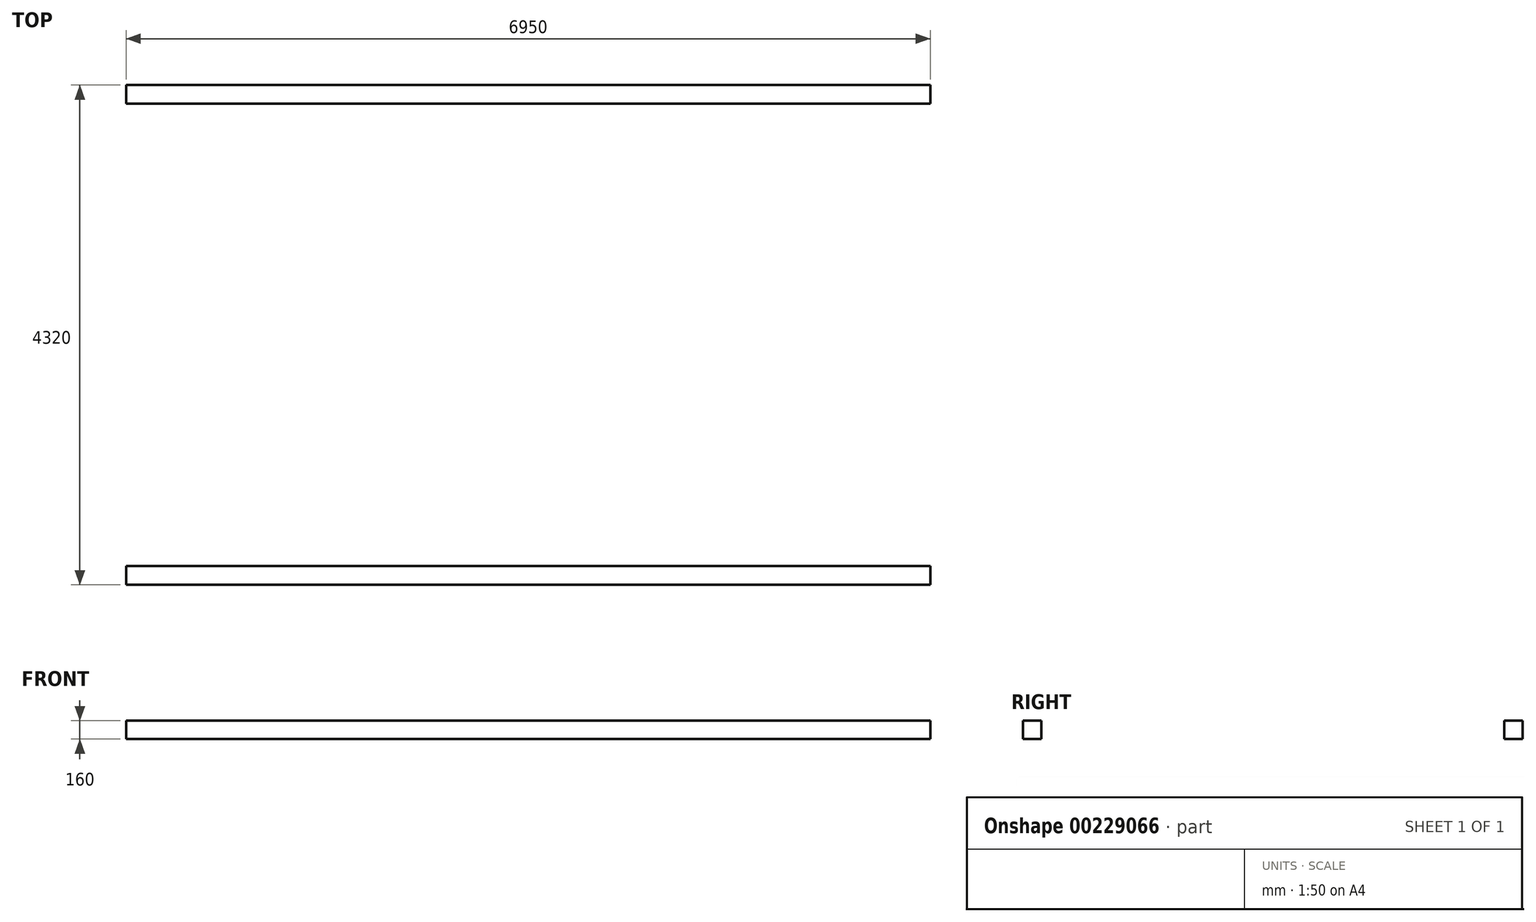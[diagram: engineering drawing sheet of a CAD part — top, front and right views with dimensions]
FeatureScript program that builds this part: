
annotation { "Feature Type Name" : "Feature", "Feature Type Description" : "" }
export const myFeature = defineFeature(function(context is Context, id is Id, definition is map)
    precondition{}
    {
        {
            var Q0;
            Q0=qCreatedBy(makeId("Top.planeOp"),FACE);
            var sketch = newSketch(context, id + "F0", { "sketchPlane" : qUnion([Q0])});
            skLineSegment(sketch, "E0.bottom", {"start": v(-39.6, 45.34) * mm, "end": v(61.47, 45.34) * mm});
            skLineSegment(sketch, "E0.top", {"start": v(-39.6, 50.14) * mm, "end": v(61.47, 50.14) * mm});
            skLineSegment(sketch, "E0.left", {"start": v(-39.6, 45.34) * mm, "end": v(-39.6, 50.14) * mm});
            skLineSegment(sketch, "E0.right", {"start": v(61.47, 45.34) * mm, "end": v(61.47, 50.14) * mm});
            skLineSegment(sketch, "E1.bottom", {"start": v(-39.6, 11.73) * mm, "end": v(61.47, 11.73) * mm});
            skLineSegment(sketch, "E1.top", {"start": v(-39.6, 16) * mm, "end": v(61.47, 16) * mm});
            skLineSegment(sketch, "E1.left", {"start": v(-39.6, 11.73) * mm, "end": v(-39.6, 16) * mm});
            skLineSegment(sketch, "E1.right", {"start": v(61.47, 11.73) * mm, "end": v(61.47, 16) * mm});
            skSolve(sketch);
        }
        {
            var Q0;
            Q0=makeQuery(id+"F0.imprint","IMPRINT",FACE,{"disambiguationData":[TD([[makeQuery(id+"F0.imprint","IMPRINT",EDGE,{"derivedFrom":sQuery(id+"F0.wireOp",EDGE,"E0.bottom")}),1.0]])]});
            var Q1;
            Q1=makeQuery(id+"F0.imprint","IMPRINT",FACE,{"disambiguationData":[TD([[makeQuery(id+"F0.imprint","IMPRINT",EDGE,{"derivedFrom":sQuery(id+"F0.wireOp",EDGE,"E1.bottom")}),1.0]])]});
            extrude(context, id + "F1", {"entities" : qUnion([Q0, Q1]), "depth" : 152.4 * mm});
        }
        {
            var Q0;
            Q0=makeQuery(id+"F1.opExtrude","SWEPT_BODY",BODY,{"disambiguationData":[OSD([sQuery(id+"F0.wireOp",EDGE,"E0.bottom"),sQuery(id+"F0.wireOp",EDGE,"E0.top"),sQuery(id+"F0.wireOp",EDGE,"E0.left"),sQuery(id+"F0.wireOp",EDGE,"E0.right")])]});
            var Q1;
            Q1=makeQuery(id+"F1.opExtrude","SWEPT_BODY",BODY,{"disambiguationData":[OSD([sQuery(id+"F0.wireOp",EDGE,"E1.bottom"),sQuery(id+"F0.wireOp",EDGE,"E1.top"),sQuery(id+"F0.wireOp",EDGE,"E1.left"),sQuery(id+"F0.wireOp",EDGE,"E1.right")])]});
            deleteBodies(context, id + "F2", {"entities" : qUnion([Q0, Q1])});
        }
        {
            var Q0;
            Q0=qCreatedBy(makeId("Top.planeOp"),FACE);
            var sketch = newSketch(context, id + "F3", { "sketchPlane" : qUnion([Q0])});
            skLineSegment(sketch, "E2.bottom", {"start": v(-675.07, 105.87) * mm, "end": v(6274.93, 105.87) * mm});
            skLineSegment(sketch, "E2.top", {"start": v(-675.07, -54.13) * mm, "end": v(6274.93, -54.13) * mm});
            skLineSegment(sketch, "E2.left", {"start": v(-675.07, 105.87) * mm, "end": v(-675.07, -54.13) * mm});
            skLineSegment(sketch, "E2.right", {"start": v(6274.93, 105.87) * mm, "end": v(6274.93, -54.13) * mm});
            skLineSegment(sketch, "E3", {"start": v(-675.07, 4105.87) * mm, "end": v(-675.07, 4265.87) * mm});
            skLineSegment(sketch, "E4", {"start": v(-675.07, 4265.87) * mm, "end": v(6274.93, 4265.87) * mm});
            skLineSegment(sketch, "E5", {"start": v(6274.93, 4265.87) * mm, "end": v(6274.93, 4105.87) * mm});
            skLineSegment(sketch, "E6", {"start": v(6274.93, 4105.87) * mm, "end": v(-675.07, 4105.87) * mm});
            skSolve(sketch);
        }
        {
            var Q0;
            Q0=makeQuery(id+"F3.imprint","IMPRINT",FACE,{"disambiguationData":[TD([[makeQuery(id+"F3.imprint","IMPRINT",EDGE,{"derivedFrom":sQuery(id+"F3.wireOp",EDGE,"E3")}),-1.0]])]});
            var Q1;
            Q1=makeQuery(id+"F3.imprint","IMPRINT",FACE,{"disambiguationData":[TD([[makeQuery(id+"F3.imprint","IMPRINT",EDGE,{"derivedFrom":sQuery(id+"F3.wireOp",EDGE,"E2.bottom")}),-1.0]])]});
            extrude(context, id + "F4", {"entities" : qUnion([Q0, Q1]), "depth" : 160 * mm});
        }
    });
